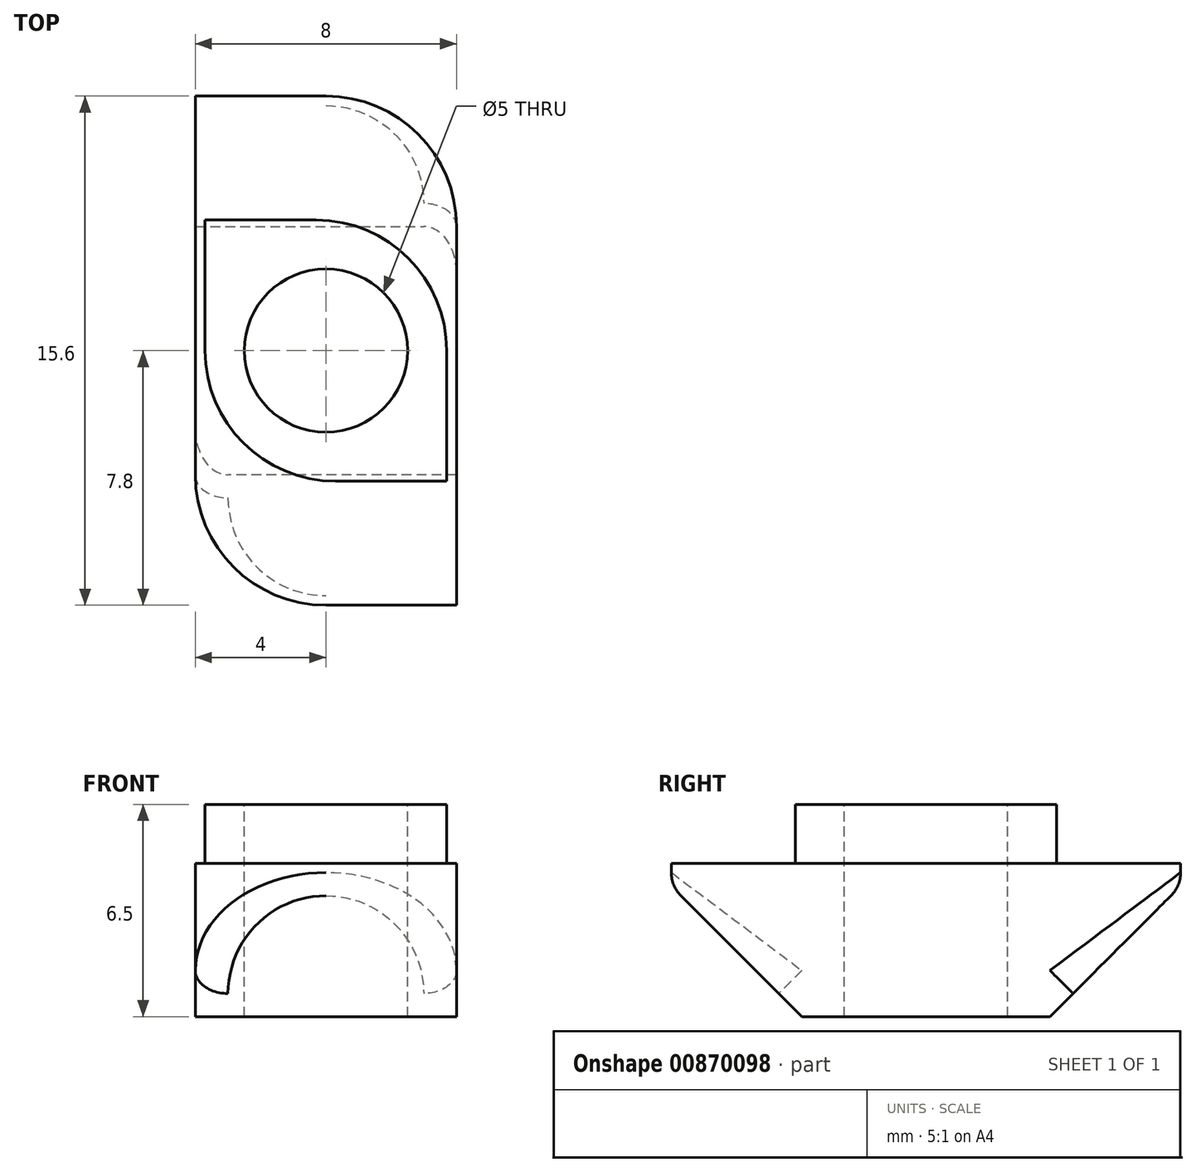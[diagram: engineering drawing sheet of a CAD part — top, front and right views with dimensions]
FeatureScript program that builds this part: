
annotation { "Feature Type Name" : "Feature", "Feature Type Description" : "" }
export const myFeature = defineFeature(function(context is Context, id is Id, definition is map)
    precondition{}
    {
        {
            var Q0;
            Q0=qCreatedBy(makeId("Top.planeOp"),FACE);
            var sketch = newSketch(context, id + "F0", { "sketchPlane" : qUnion([Q0])});
            skLineSegment(sketch, "E0.bottom", {"start": v(4, -7.8) * mm, "end": v(0, -7.8) * mm});
            skLineSegment(sketch, "E0.top", {"start": v(0, 7.8) * mm, "end": v(-4, 7.8) * mm});
            skLineSegment(sketch, "E0.left", {"start": v(4, -7.8) * mm, "end": v(4, 3.8) * mm});
            skLineSegment(sketch, "E0.right", {"start": v(-4, -3.8) * mm, "end": v(-4, 7.8) * mm});
            skPoint(sketch, "E0.middle", {"position": v(0, 0) * mm});
            skPoint(sketch, "E1.visualSharp", {"position": v(4, 7.8) * mm});
            skArc(sketch, "E1.filletArc", {"start": v(4, 3.8) * mm, "mid": v(2.83, 6.63) * mm, "end": v(0, 7.8) * mm});
            skPoint(sketch, "E2.visualSharp", {"position": v(-4, -7.8) * mm});
            skArc(sketch, "E2.filletArc", {"start": v(-4, -3.8) * mm, "mid": v(-2.83, -6.63) * mm, "end": v(0, -7.8) * mm});
            skSolve(sketch);
        }
        {
            var Q0;
            Q0 = qSketchRegion(id + "F0", true);
            extrude(context, id + "F1", {"entities" : qUnion([Q0]), "oppositeDirection" : true, "depth" : 4.7 * mm, "offsetDistance" : 25 * mm});
        }
        {
            var Q0;
            Q0=makeQuery(id+"F1.opExtrude","CAP_FACE",FACE,{"disambiguationData":[OSD([sQuery(id+"F0.wireOp",EDGE,"E0.bottom"),sQuery(id+"F0.wireOp",EDGE,"E0.top"),sQuery(id+"F0.wireOp",EDGE,"E0.left"),sQuery(id+"F0.wireOp",EDGE,"E0.right"),sQuery(id+"F0.wireOp",EDGE,"E1.filletArc"),sQuery(id+"F0.wireOp",EDGE,"E2.filletArc")])],"isStart":true});
            var sketch = newSketch(context, id + "F2", { "sketchPlane" : qUnion([Q0])});
            skSolve(sketch);
        }
        {
            var Q0;
            Q0=makeQuery(id+"F2.imprint","IMPRINT",FACE,{"disambiguationData":[TD([[makeQuery(id+"F2.imprint","IMPRINT",EDGE,{"derivedFrom":makeQuery(id+"F1.opExtrude","CAP_EDGE",EDGE,{"disambiguationData":[OSD([sQuery(id+"F0.wireOp",EDGE,"E0.bottom")])],"isStart":true})}),-1.0]])]});
            var sketch = newSketch(context, id + "F3", { "sketchPlane" : qUnion([Q0])});
            skLineSegment(sketch, "E3.bottom", {"start": v(3.7, -4) * mm, "end": v(0.3, -4) * mm});
            skLineSegment(sketch, "E3.top", {"start": v(-0.3, 4) * mm, "end": v(-3.7, 4) * mm});
            skLineSegment(sketch, "E3.left", {"start": v(3.7, -4) * mm, "end": v(3.7, 0) * mm});
            skLineSegment(sketch, "E3.right", {"start": v(-3.7, 0) * mm, "end": v(-3.7, 4) * mm});
            skPoint(sketch, "E3.middle", {"position": v(0, 0) * mm});
            skPoint(sketch, "E4.visualSharp", {"position": v(3.7, 4) * mm});
            skArc(sketch, "E4.filletArc", {"start": v(3.7, 0) * mm, "mid": v(2.53, 2.83) * mm, "end": v(-0.3, 4) * mm});
            skPoint(sketch, "E5.visualSharp", {"position": v(-3.7, -4) * mm});
            skArc(sketch, "E5.filletArc", {"start": v(-3.7, 0) * mm, "mid": v(-2.53, -2.83) * mm, "end": v(0.3, -4) * mm});
            skSolve(sketch);
        }
        {
            var Q0;
            Q0 = qSketchRegion(id + "F3", true);
            extrude(context, id + "F4", {"entities" : qUnion([Q0]), "operationType" : NewBodyOperationType.ADD, "depth" : 1.8 * mm, "offsetDistance" : 25 * mm});
        }
        {
            var Q0;
            Q0=makeQuery(id+"F1.opExtrude","CAP_EDGE",EDGE,{"disambiguationData":[OSD([sQuery(id+"F0.wireOp",EDGE,"E0.top")])],"isStart":false});
            var Q1;
            Q1=makeQuery(id+"F1.opExtrude","CAP_EDGE",EDGE,{"disambiguationData":[OSD([sQuery(id+"F0.wireOp",EDGE,"E0.bottom")])],"isStart":false});
            chamfer(context, id + "F5", {"entities" : qUnion([Q0, Q1]), "width" : 4 * mm});
        }
        {
            var Q0;
            Q0=makeQuery(id+"F5.opChamfer","BLEND_EDGE",EDGE,{"blendedFrom":[makeQuery(id+"F1.opExtrude","CAP_EDGE",EDGE,{"disambiguationData":[OSD([sQuery(id+"F0.wireOp",EDGE,"E0.top")])],"isStart":false}),makeQuery(id+"F1.opExtrude","SWEPT_FACE",FACE,{"disambiguationData":[OSD([sQuery(id+"F0.wireOp",EDGE,"E1.filletArc")])]})],"blendedInto":[makeQuery(id+"F1.opExtrude","SWEPT_FACE",FACE,{"disambiguationData":[OSD([sQuery(id+"F0.wireOp",EDGE,"E1.filletArc")])]})]});
            var Q1;
            Q1=makeQuery(id+"F5.opChamfer","BLEND_EDGE",EDGE,{"blendedFrom":[makeQuery(id+"F1.opExtrude","CAP_EDGE",EDGE,{"disambiguationData":[OSD([sQuery(id+"F0.wireOp",EDGE,"E0.bottom")])],"isStart":false}),makeQuery(id+"F1.opExtrude","SWEPT_FACE",FACE,{"disambiguationData":[OSD([sQuery(id+"F0.wireOp",EDGE,"E2.filletArc")])]})],"blendedInto":[makeQuery(id+"F1.opExtrude","SWEPT_FACE",FACE,{"disambiguationData":[OSD([sQuery(id+"F0.wireOp",EDGE,"E2.filletArc")])]})]});
            fillet(context, id + "F6", {"entities" : qUnion([Q0, Q1]), "radius" : 1 * mm, "tangentPropagation" : true, "allowEdgeOverflow" : false});
        }
        {
            var Q0;
            Q0=makeQuery(id+"F4.opExtrude","CAP_FACE",FACE,{"disambiguationData":[OSD([sQuery(id+"F3.wireOp",EDGE,"E3.bottom"),sQuery(id+"F3.wireOp",EDGE,"E3.top"),sQuery(id+"F3.wireOp",EDGE,"E3.left"),sQuery(id+"F3.wireOp",EDGE,"E3.right"),sQuery(id+"F3.wireOp",EDGE,"E4.filletArc"),sQuery(id+"F3.wireOp",EDGE,"E5.filletArc")])],"isStart":false});
            var sketch = newSketch(context, id + "F7", { "sketchPlane" : qUnion([Q0])});
            skPoint(sketch, "E6", {"position": v(0, 0) * mm});
            skSolve(sketch);
        }
        {
            var Q0;
            Q0=sQuery(id+"F7.wireOp",VERTEX,"E6");
            var Q1;
            Q1=makeQuery(id+"F1.opExtrude","SWEPT_BODY",BODY,{"disambiguationData":[OSD([sQuery(id+"F0.wireOp",EDGE,"E0.bottom"),sQuery(id+"F0.wireOp",EDGE,"E0.top"),sQuery(id+"F0.wireOp",EDGE,"E0.left"),sQuery(id+"F0.wireOp",EDGE,"E0.right"),sQuery(id+"F0.wireOp",EDGE,"E1.filletArc"),sQuery(id+"F0.wireOp",EDGE,"E2.filletArc")])]});
            hole(context, id + "F8", {"style" : HoleStyle.SIMPLE, "endStyle" : HoleEndStyle.THROUGH, "standardTappedOrClearance" : lookupTablePath({ "standard" : "ISO", "engagement" : "75%", "pitch" : "1 mm", "size" : "M6", "type" : "Tapped" }), "standardBlindInLast" : lookupTablePath({ "standard" : "ISO", "engagement" : "75%", "pitch" : "1 mm", "size" : "M6", "type" : "Tapped" }), "holeDiameter" : 5 * mm, "majorDiameter" : 6 * mm, "showTappedDepth" : true, "isTappedThrough" : true, "tappedDepth" : 8.5 * mm, "tapClearance" : 3, "startFromSketch" : true, "locations" : qUnion([Q0]), "scope" : qUnion([Q1])});
        }
    });
